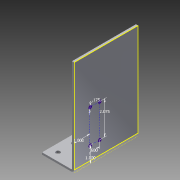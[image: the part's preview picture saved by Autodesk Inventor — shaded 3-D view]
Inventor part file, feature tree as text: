
AUTODESK INVENTOR PART (.ipt)
format: ipt  version: 2013 (Build 170138000, 138)  size: 119,296 bytes
history: native  units: in
note: dims shown in document units (in); Inventor stores cm internally (conversion verified against a paired STEP export)
features: sheet_metal_op x4, sketch x3, other x2
ambient origin geometry x8: Origin, YZ Plane, XZ Plane, XY Plane, X Axis, Y Axis, Z Axis, Center Point
bodies: Solid1 (feature_tree)
feature tree (9):
  sheet_metal_op  "Face1"
  sheet_metal_op  "Flange1"
  sketch  "Sketch3"  dims[d3=0.26in d4=1.0in d5=2.0in d6=0.5in d7=0.125in d8=1.0in d9=0.125in d10=0.0625in d11=0.25in d12=0.125in d13=6.0in d14=90.0deg d15=0.05in d16=0.5in d17=0.125in d18=0.125in d19=2.075in d21=0.6in d22=0.175in d23=1.0in d24=1.0in]
  sketch  "Sketch1"  dims[d0=4.0in]
  other  "Plate1"
  sketch  "Sketch2"  dims[d2=1.0in]
  other  "Plate2"
  sheet_metal_op  "Bend1"
  sheet_metal_op  "Corner1"
